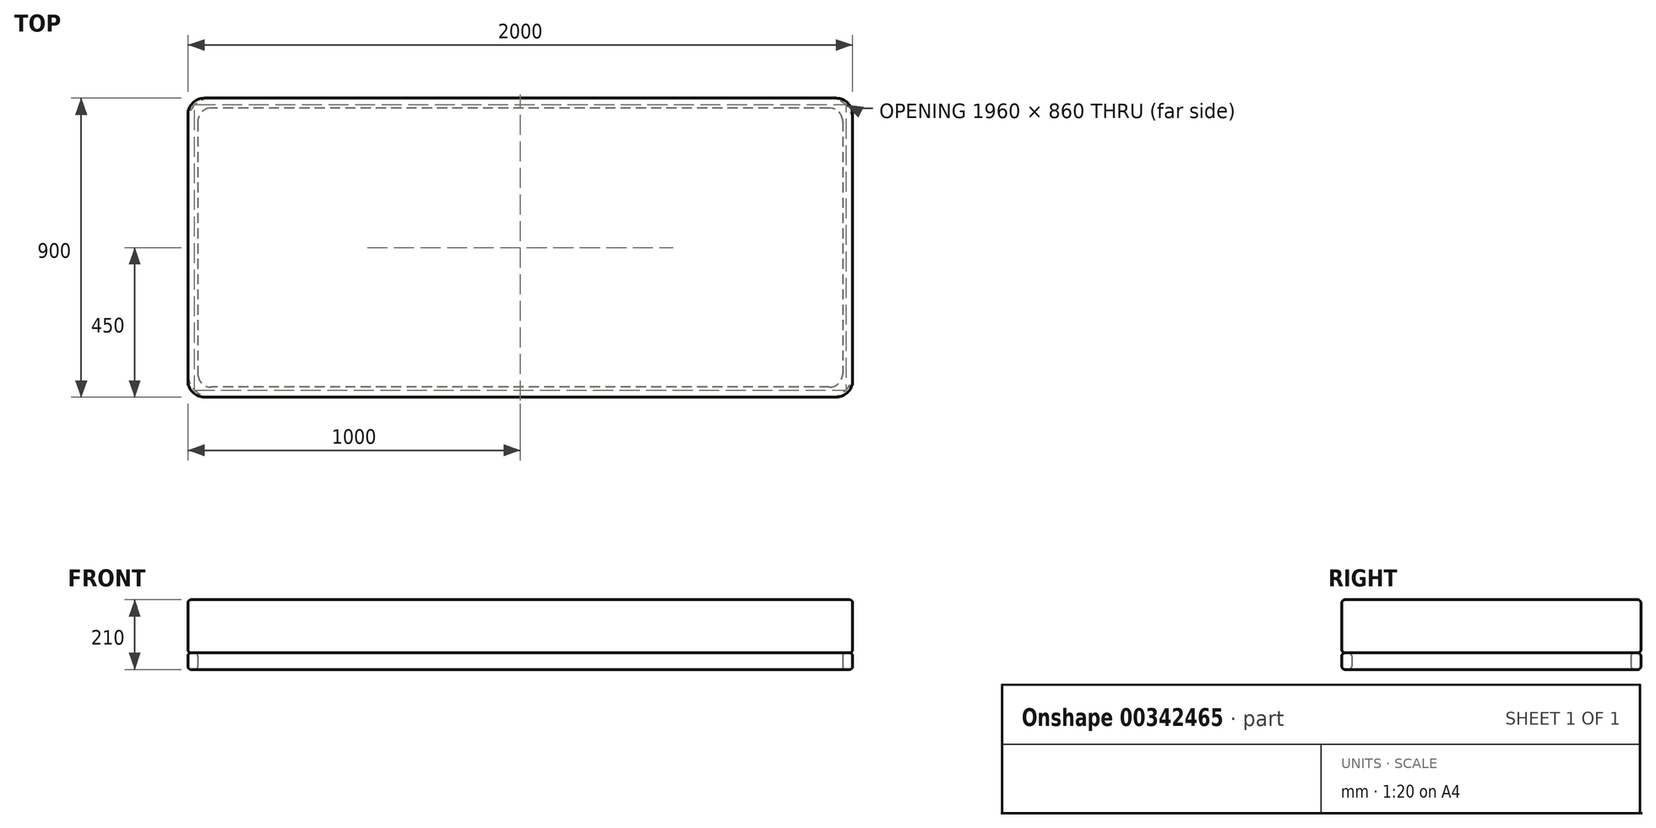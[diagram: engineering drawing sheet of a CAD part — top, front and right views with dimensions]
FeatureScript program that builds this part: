
annotation { "Feature Type Name" : "Feature", "Feature Type Description" : "" }
export const myFeature = defineFeature(function(context is Context, id is Id, definition is map)
    precondition{}
    {
        {
            var Q0;
            Q0=qCreatedBy(makeId("Top.planeOp"),FACE);
            var sketch = newSketch(context, id + "F0", { "sketchPlane" : qUnion([Q0])});
            skLineSegment(sketch, "E0.bottom", {"start": v(-1000, 450) * mm, "end": v(1000, 450) * mm});
            skLineSegment(sketch, "E0.top", {"start": v(-1000, -450) * mm, "end": v(1000, -450) * mm});
            skLineSegment(sketch, "E0.left", {"start": v(-1000, 450) * mm, "end": v(-1000, -450) * mm});
            skLineSegment(sketch, "E0.right", {"start": v(1000, 450) * mm, "end": v(1000, -450) * mm});
            skPoint(sketch, "E0.middle", {"position": v(0, 0) * mm});
            skSolve(sketch);
        }
        {
            var Q0;
            Q0 = qSketchRegion(id + "F0", true);
            extrude(context, id + "F1", {"entities" : qUnion([Q0]), "depth" : 160 * mm});
        }
        {
            var Q0;
            Q0=makeQuery(id+"F1.opExtrude","SWEPT_EDGE",EDGE,{"disambiguationData":[OSD([sQuery(id+"F0.wireOp",EDGE,"E0.top"),sQuery(id+"F0.wireOp",EDGE,"E0.left")])]});
            var Q1;
            Q1=makeQuery(id+"F1.opExtrude","SWEPT_EDGE",EDGE,{"disambiguationData":[OSD([sQuery(id+"F0.wireOp",EDGE,"E0.top"),sQuery(id+"F0.wireOp",EDGE,"E0.right")])]});
            var Q2;
            Q2=makeQuery(id+"F1.opExtrude","SWEPT_EDGE",EDGE,{"disambiguationData":[OSD([sQuery(id+"F0.wireOp",EDGE,"E0.bottom"),sQuery(id+"F0.wireOp",EDGE,"E0.right")])]});
            var Q3;
            Q3=makeQuery(id+"F1.opExtrude","SWEPT_EDGE",EDGE,{"disambiguationData":[OSD([sQuery(id+"F0.wireOp",EDGE,"E0.bottom"),sQuery(id+"F0.wireOp",EDGE,"E0.left")])]});
            fillet(context, id + "F2", {"entities" : qUnion([Q0, Q1, Q2, Q3]), "radius" : 50 * mm, "tangentPropagation" : true, "allowEdgeOverflow" : false});
        }
        {
            var Q0;
            Q0=makeQuery(id+"F1.opExtrude","CAP_FACE",FACE,{"disambiguationData":[OSD([sQuery(id+"F0.wireOp",EDGE,"E0.bottom"),sQuery(id+"F0.wireOp",EDGE,"E0.top"),sQuery(id+"F0.wireOp",EDGE,"E0.left"),sQuery(id+"F0.wireOp",EDGE,"E0.right")])],"isStart":false});
            var Q1;
            Q1=makeQuery(id+"F1.opExtrude","CAP_FACE",FACE,{"disambiguationData":[OSD([sQuery(id+"F0.wireOp",EDGE,"E0.bottom"),sQuery(id+"F0.wireOp",EDGE,"E0.top"),sQuery(id+"F0.wireOp",EDGE,"E0.left"),sQuery(id+"F0.wireOp",EDGE,"E0.right")])],"isStart":true});
            fillet(context, id + "F3", {"entities" : qUnion([Q0, Q1]), "radius" : 10 * mm, "tangentPropagation" : true, "allowEdgeOverflow" : false});
        }
        {
            var Q0;
            Q0=qCreatedBy(makeId("Top.planeOp"),FACE);
            var sketch = newSketch(context, id + "F4", { "sketchPlane" : qUnion([Q0])});
            skLineSegment(sketch, "E1.bottom", {"start": v(930, 450) * mm, "end": v(-930, 450) * mm});
            skLineSegment(sketch, "E1.top", {"start": v(930, -450) * mm, "end": v(-930, -450) * mm});
            skLineSegment(sketch, "E1.left", {"start": v(1000, 380) * mm, "end": v(1000, -380) * mm});
            skLineSegment(sketch, "E1.right", {"start": v(-1000, 380) * mm, "end": v(-1000, -380) * mm});
            skPoint(sketch, "E1.middle", {"position": v(0, 0) * mm});
            skLineSegment(sketch, "E2.bottom", {"start": v(930, 420) * mm, "end": v(-930, 420) * mm});
            skLineSegment(sketch, "E2.top", {"start": v(930, -420) * mm, "end": v(-930, -420) * mm});
            skLineSegment(sketch, "E2.left", {"start": v(970, 380) * mm, "end": v(970, -380) * mm});
            skLineSegment(sketch, "E2.right", {"start": v(-970, 380) * mm, "end": v(-970, -380) * mm});
            skPoint(sketch, "E3.visualSharp", {"position": v(-970, 420) * mm});
            skArc(sketch, "E3.filletArc", {"start": v(-930, 420) * mm, "mid": v(-958.28, 408.28) * mm, "end": v(-970, 380) * mm});
            skPoint(sketch, "E4.visualSharp", {"position": v(970, 420) * mm});
            skArc(sketch, "E4.filletArc", {"start": v(970, 380) * mm, "mid": v(958.28, 408.28) * mm, "end": v(930, 420) * mm});
            skPoint(sketch, "E5.visualSharp", {"position": v(970, -420) * mm});
            skArc(sketch, "E5.filletArc", {"start": v(930, -420) * mm, "mid": v(958.28, -408.28) * mm, "end": v(970, -380) * mm});
            skPoint(sketch, "E6.visualSharp", {"position": v(-970, -420) * mm});
            skArc(sketch, "E6.filletArc", {"start": v(-970, -380) * mm, "mid": v(-958.28, -408.28) * mm, "end": v(-930, -420) * mm});
            skPoint(sketch, "E7.visualSharp", {"position": v(-1000, 450) * mm});
            skArc(sketch, "E7.filletArc", {"start": v(-930, 450) * mm, "mid": v(-979.5, 429.5) * mm, "end": v(-1000, 380) * mm});
            skPoint(sketch, "E8.visualSharp", {"position": v(1000, 450) * mm});
            skArc(sketch, "E8.filletArc", {"start": v(1000, 380) * mm, "mid": v(979.5, 429.5) * mm, "end": v(930, 450) * mm});
            skPoint(sketch, "E9.visualSharp", {"position": v(1000, -450) * mm});
            skArc(sketch, "E9.filletArc", {"start": v(930, -450) * mm, "mid": v(979.5, -429.5) * mm, "end": v(1000, -380) * mm});
            skPoint(sketch, "E10.visualSharp", {"position": v(-1000, -450) * mm});
            skArc(sketch, "E10.filletArc", {"start": v(-1000, -380) * mm, "mid": v(-979.5, -429.5) * mm, "end": v(-930, -450) * mm});
            skSolve(sketch);
        }
        {
            var Q0;
            Q0 = qSketchRegion(id + "F4", true);
            extrude(context, id + "F5", {"entities" : qUnion([Q0]), "depth" : 50 * mm});
        }
        {
            var Q0;
            Q0=makeQuery(id+"F1.opExtrude","SWEPT_BODY",BODY,{"disambiguationData":[OSD([sQuery(id+"F0.wireOp",EDGE,"E0.bottom"),sQuery(id+"F0.wireOp",EDGE,"E0.top"),sQuery(id+"F0.wireOp",EDGE,"E0.left"),sQuery(id+"F0.wireOp",EDGE,"E0.right")])]});
            var Q1;
            {var subQ0=sQuery(id+"F0.wireOp",EDGE,"E0.top");Q1=makeQuery(id+"F2.opFillet","BLEND_EDGE",EDGE,{"blendedFrom":[makeQuery(id+"F1.opExtrude","SWEPT_EDGE",EDGE,{"disambiguationData":[OSD([subQ0,sQuery(id+"F0.wireOp",EDGE,"E0.left")])]}),makeQuery(id+"F1.opExtrude","SWEPT_FACE",FACE,{"disambiguationData":[OSD([subQ0])]})],"blendedInto":[makeQuery(id+"F1.opExtrude","SWEPT_FACE",FACE,{"disambiguationData":[OSD([subQ0])]})]});}
            transform(context, id + "F6", {"entities" : qUnion([Q0]), "transformType" : TransformType.TRANSLATION_DISTANCE, "transformDirection" : qUnion([Q1]), "distance" : 50 * mm, "oppositeDirection" : true, "makeCopy" : false});
        }
        {
            var Q0;
            Q0=makeQuery(id+"F5.opExtrude","CAP_FACE",FACE,{"disambiguationData":[OSD([sQuery(id+"F4.wireOp",EDGE,"E1.bottom"),sQuery(id+"F4.wireOp",EDGE,"E1.top"),sQuery(id+"F4.wireOp",EDGE,"E1.left"),sQuery(id+"F4.wireOp",EDGE,"E1.right"),sQuery(id+"F4.wireOp",EDGE,"E2.bottom"),sQuery(id+"F4.wireOp",EDGE,"E2.top"),sQuery(id+"F4.wireOp",EDGE,"E2.left"),sQuery(id+"F4.wireOp",EDGE,"E2.right"),sQuery(id+"F4.wireOp",EDGE,"E3.filletArc"),sQuery(id+"F4.wireOp",EDGE,"E4.filletArc"),sQuery(id+"F4.wireOp",EDGE,"E5.filletArc"),sQuery(id+"F4.wireOp",EDGE,"E6.filletArc"),sQuery(id+"F4.wireOp",EDGE,"E7.filletArc"),sQuery(id+"F4.wireOp",EDGE,"E8.filletArc"),sQuery(id+"F4.wireOp",EDGE,"E9.filletArc"),sQuery(id+"F4.wireOp",EDGE,"E10.filletArc")])],"isStart":false});
            var Q1;
            Q1=makeQuery(id+"F5.opExtrude","CAP_FACE",FACE,{"disambiguationData":[OSD([sQuery(id+"F4.wireOp",EDGE,"E1.bottom"),sQuery(id+"F4.wireOp",EDGE,"E1.top"),sQuery(id+"F4.wireOp",EDGE,"E1.left"),sQuery(id+"F4.wireOp",EDGE,"E1.right"),sQuery(id+"F4.wireOp",EDGE,"E2.bottom"),sQuery(id+"F4.wireOp",EDGE,"E2.top"),sQuery(id+"F4.wireOp",EDGE,"E2.left"),sQuery(id+"F4.wireOp",EDGE,"E2.right"),sQuery(id+"F4.wireOp",EDGE,"E3.filletArc"),sQuery(id+"F4.wireOp",EDGE,"E4.filletArc"),sQuery(id+"F4.wireOp",EDGE,"E5.filletArc"),sQuery(id+"F4.wireOp",EDGE,"E6.filletArc"),sQuery(id+"F4.wireOp",EDGE,"E7.filletArc"),sQuery(id+"F4.wireOp",EDGE,"E8.filletArc"),sQuery(id+"F4.wireOp",EDGE,"E9.filletArc"),sQuery(id+"F4.wireOp",EDGE,"E10.filletArc")])],"isStart":true});
            fillet(context, id + "F7", {"entities" : qUnion([Q0, Q1]), "radius" : 10 * mm, "tangentPropagation" : true, "allowEdgeOverflow" : false});
        }
    });
